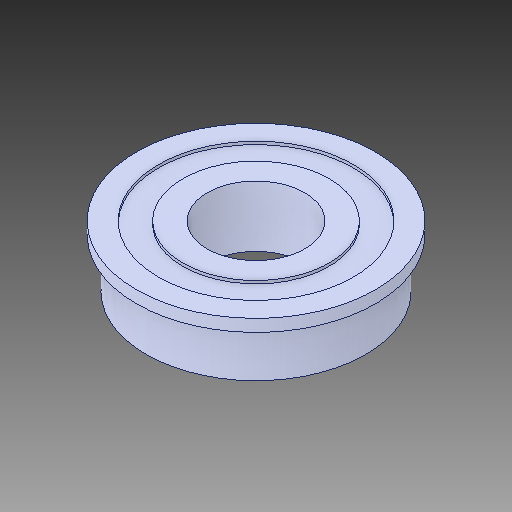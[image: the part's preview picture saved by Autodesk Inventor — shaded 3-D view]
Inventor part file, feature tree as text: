
AUTODESK INVENTOR PART (.ipt)
format: ipt  version: 2019 (Build 230136000, 136)  size: 123,392 bytes
history: native  units: in
note: dims shown in document units (in); Inventor stores cm internally (conversion verified against a paired STEP export)
features: revolve x1
ambient origin geometry x8: Origin, YZ Plane, XZ Plane, XY Plane, X Axis, Y Axis, Z Axis, Center Point
bodies: Solid1 (feature_tree)
feature tree (1):
  revolve  "Revolve1"  [1 undecoded]
note: 1 required parameter value undecoded (feature->parameter linkage not recoverable at this tier; creation-order binding heuristic only, values carry confidence <= 0.55)
